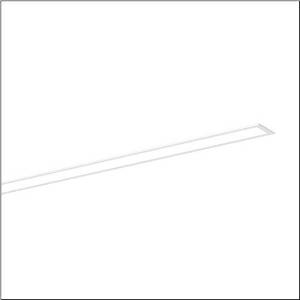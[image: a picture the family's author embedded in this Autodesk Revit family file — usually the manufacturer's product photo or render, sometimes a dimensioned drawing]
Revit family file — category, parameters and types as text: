
# Revit family: silica_21_51mx10dn35wb
name_source: partatom
category: Lighting Fixtures
units: mm (PartAtom-declared; Revit-internal decimal feet)

## family parameters
Cut with Voids When Loaded = No
Host = Face
Light Source = No
Part Type = Normal
Room Calculation Point = No
Round Connector Dimension = Use Diameter
Shared = No

## types (1)
- --- (1 x LED, 5400 lm, 37.4 W, 3000K)
    Apparent Load = 37 VA
    CIE Flux Codes = 48 79 96 100 100
    Color Rendering = 80
    Color Temperature = 3000K
    Default Elevation = 1800 mm
    Description = Silica 21, office luminaire, primary optical cover: prismatic diffuser, of PMMA, CAT 2 (L<= 3000cd/m²), light emission: direct distribution, primary light characteristic: symmetric, installation type: recessed, LED, rated luminous flux: 5.400lm, luminous efficacy: 144lm/W, light colour: 830, colour temperature: 3000K, control gear: DALI 2, with terminal, 3+2-pole, max. 2.5mm², mains connection: 220..240V, AC, 50/60Hz, rated input power: 37.4W, luminaire housing, of aluminium, traffic white (RAL 9016), length: 2.728mm, width: 79mm, height: 53mm, protection rating (complete): IP20, insulation class (complete): insulation class I (protective earthing), certification: CE, ENEC, VDE, permissible operating ambient temperature: 0..+35°C, standard: EN 50419, packaging unit: 1 piece
    Height = 0 mm  [stored 0 ft]
    Lamp = 1 x LED
    Lamp Light Flux = 5400 lm
    Lamp Power = 37.4 W
    Lamp count = 1
    Length = 2727 mm
    Luminous efficacy = 144 lm/W
    Manufacturer = Siteco
    ModVariant = No
    Model = 51MX10DN35WB
    Mounting Place = Ceiling
    Mounting Type = Recessed
    Number of Poles = 1
    OnlyDefault = Yes
    Power Factor = 1
    Product Name = Silica 21
    Product group = office luminaire | ceiling recessed
    ProductGroupID = 400
    Protection Class = Protection class I
    Protection Degree = IP 20
    RLX_Detail_Level = 1
    RLX_Emergency_Light_Flux = 0 lm
    RLX_Emergency_Type = 0
    RLX_Emergency_Type_DB = No
    RlxData = <blob elided: 21449 chars, md5=18d58112>
    Socket = socket
    Standby Power = 0 W
    System Light Flux = 5400 lm
    System Power = 37 W
    Type Comments = factory setting: luminous flux: 100 % | dim-lin: 254 | 233 mA
    Type Image = l_1335891.jpg
    URL = http://relux.com
    VarID = @adj_070249
    Voltage = 0 V
    Weight = 0.00 kg
    Width = 79 mm

note: [stored X ft] marks values corroborated as IEEE doubles in the binary element streams (Revit-internal decimal feet)

## geometry (parser evidence)
native form markers: Blend x4, Sweep x11
no freeform markers — native parametric forms only
